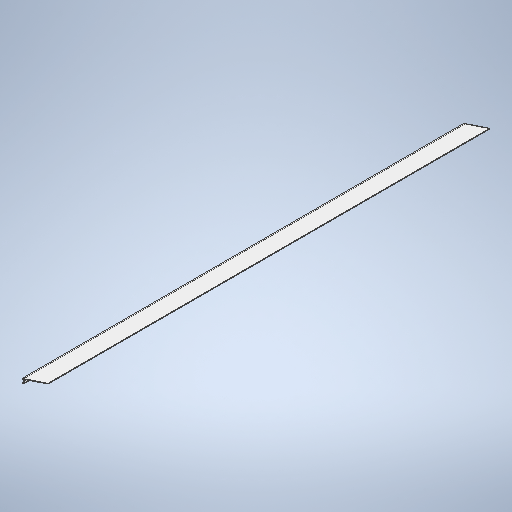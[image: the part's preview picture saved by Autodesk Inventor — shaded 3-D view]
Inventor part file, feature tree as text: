
AUTODESK INVENTOR PART (.ipt)
format: ipt  version: 2025 (Build 290162010, 162A)  size: 279,552 bytes
history: native  units: in
note: dims shown in document units (in); Inventor stores cm internally (conversion verified against a paired STEP export)
features: extrude x1, sketch x1
ambient origin geometry x8: Origin, YZ Plane, XZ Plane, XY Plane, X Axis, Y Axis, Z Axis, Center Point
bodies: Body1 (feature_tree)
feature tree (2):
  extrude  "Extrusion2"  Depth=97.504in
  sketch  "Sketch1"  dims[d5=5.5in d17=3.5in d19=132.0in d23=1.194in d28=1.8188in d33=42.875in d36=1.0in d37=0.625in d49=0.125in d50=0.125in d51=0.125in d52=0.125in d54=0.333in d55=0.333in d59=97.504in d60=0.0in d61=0.333in d62=6.0in]
